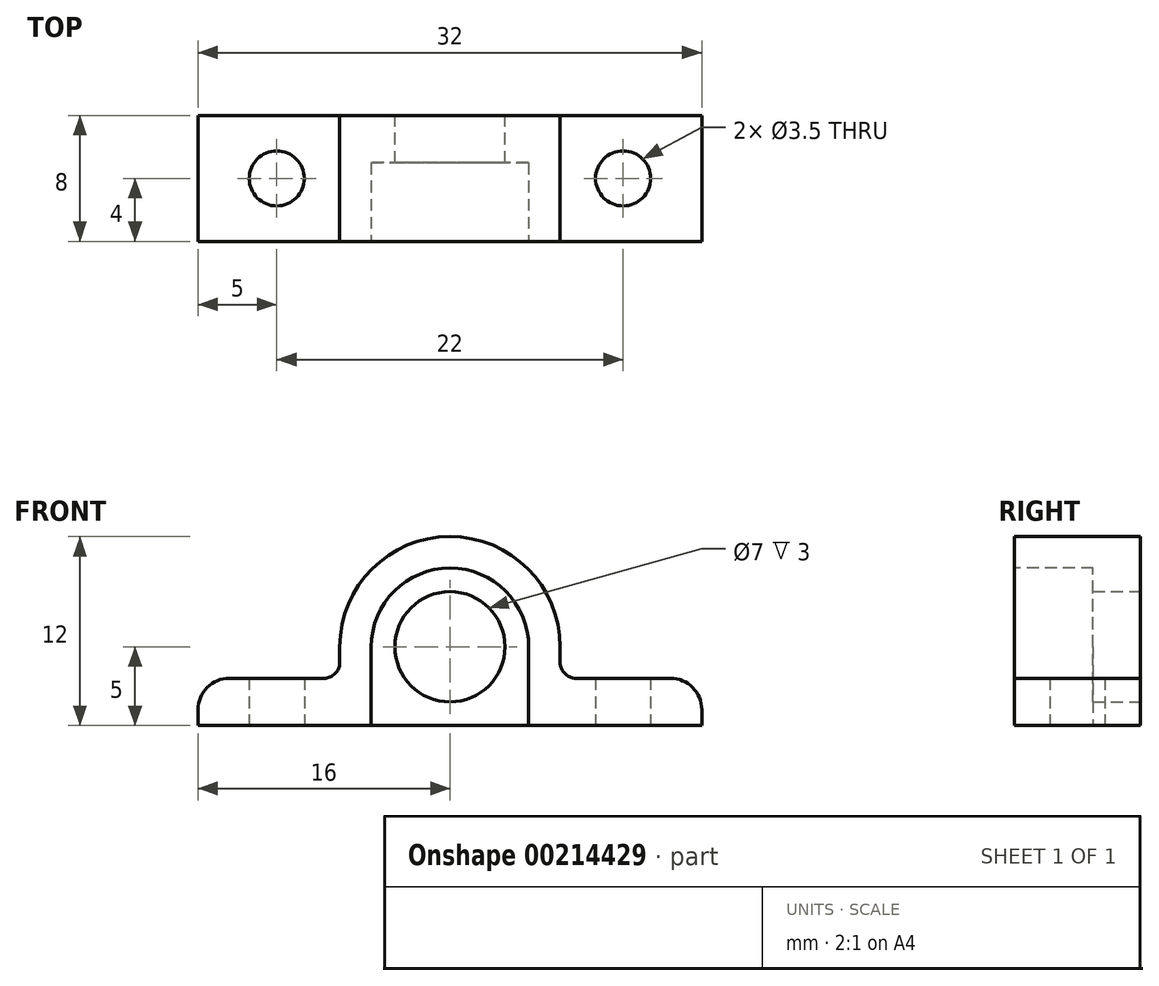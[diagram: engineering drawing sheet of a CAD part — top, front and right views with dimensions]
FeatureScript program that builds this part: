
annotation { "Feature Type Name" : "Feature", "Feature Type Description" : "" }
export const myFeature = defineFeature(function(context is Context, id is Id, definition is map)
    precondition{}
    {
        {
            var Q0;
            Q0=qCreatedBy(makeId("Front.planeOp"),FACE);
            var sketch = newSketch(context, id + "F0", { "sketchPlane" : qUnion([Q0])});
            skLineSegment(sketch, "E0.bottom", {"start": v(-16, 0) * mm, "end": v(16, 0) * mm});
            skLineSegment(sketch, "E0.top", {"start": v(0, 12) * mm, "end": v(0, 12) * mm});
            skLineSegment(sketch, "E0.left", {"start": v(-16, 0) * mm, "end": v(-16, 1) * mm});
            skLineSegment(sketch, "E0.right", {"start": v(16, 0) * mm, "end": v(16, 1) * mm});
            skCircle(sketch, "E1", {"center": v(0, 5) * mm, "radius": 3.5 * mm});
            skLineSegment(sketch, "E2.top", {"start": v(-14, 3) * mm, "end": v(-8, 3) * mm});
            skLineSegment(sketch, "E2.right", {"start": v(-7, 5) * mm, "end": v(-7, 4) * mm});
            skLineSegment(sketch, "E3.top", {"start": v(14, 3) * mm, "end": v(8, 3) * mm});
            skLineSegment(sketch, "E3.right", {"start": v(7, 5) * mm, "end": v(7, 4) * mm});
            skPoint(sketch, "E4.visualSharp", {"position": v(-7, 12) * mm});
            skArc(sketch, "E4.filletArc", {"start": v(0, 12) * mm, "mid": v(-4.95, 9.95) * mm, "end": v(-7, 5) * mm});
            skPoint(sketch, "E5.visualSharp", {"position": v(7, 12) * mm});
            skArc(sketch, "E5.filletArc", {"start": v(7, 5) * mm, "mid": v(4.95, 9.95) * mm, "end": v(0, 12) * mm});
            skPoint(sketch, "E6.visualSharp", {"position": v(-7, 3) * mm});
            skArc(sketch, "E6.filletArc", {"start": v(-8, 3) * mm, "mid": v(-7.3, 3.3) * mm, "end": v(-7, 4) * mm});
            skPoint(sketch, "E7.visualSharp", {"position": v(7, 3) * mm});
            skArc(sketch, "E7.filletArc", {"start": v(7, 4) * mm, "mid": v(7.3, 3.3) * mm, "end": v(8, 3) * mm});
            skPoint(sketch, "E8.visualSharp", {"position": v(-16, 3) * mm});
            skArc(sketch, "E8.filletArc", {"start": v(-14, 3) * mm, "mid": v(-15.41, 2.41) * mm, "end": v(-16, 1) * mm});
            skPoint(sketch, "E9.visualSharp", {"position": v(16, 3) * mm});
            skArc(sketch, "E9.filletArc", {"start": v(16, 1) * mm, "mid": v(15.41, 2.41) * mm, "end": v(14, 3) * mm});
            skSolve(sketch);
        }
        {
            var Q0;
            Q0=makeQuery(id+"F0.imprint","IMPRINT",FACE,{"disambiguationData":[TD([[makeQuery(id+"F0.imprint","IMPRINT",EDGE,{"derivedFrom":sQuery(id+"F0.wireOp",EDGE,"E0.bottom")}),1.0]])]});
            extrude(context, id + "F1", {"entities" : qUnion([Q0]), "depth" : 8 * mm});
        }
        {
            var Q0;
            Q0=makeQuery(id+"F1.opExtrude","SWEPT_FACE",FACE,{"disambiguationData":[OSD([sQuery(id+"F0.wireOp",EDGE,"E0.bottom")])]});
            var sketch = newSketch(context, id + "F2", { "sketchPlane" : qUnion([Q0])});
            skCircle(sketch, "E10", {"center": v(-11, 4) * mm, "radius": 1.75 * mm});
            skCircle(sketch, "E11", {"center": v(11, 4) * mm, "radius": 1.75 * mm});
            skSolve(sketch);
        }
        {
            var Q0;
            Q0 = qSketchRegion(id + "F2", true);
            extrude(context, id + "F3", {"entities" : qUnion([Q0]), "operationType" : NewBodyOperationType.REMOVE, "endBound" : BoundingType.THROUGH_ALL, "oppositeDirection" : true, "depth" : 25 * mm});
        }
        {
            var Q0;
            Q0=makeQuery(id+"F1.opExtrude","CAP_FACE",FACE,{"disambiguationData":[OSD([sQuery(id+"F0.wireOp",EDGE,"E0.bottom"),sQuery(id+"F0.wireOp",EDGE,"E0.left"),sQuery(id+"F0.wireOp",EDGE,"E0.right"),sQuery(id+"F0.wireOp",EDGE,"E1"),sQuery(id+"F0.wireOp",EDGE,"E2.top"),sQuery(id+"F0.wireOp",EDGE,"E2.right"),sQuery(id+"F0.wireOp",EDGE,"E3.top"),sQuery(id+"F0.wireOp",EDGE,"E3.right"),sQuery(id+"F0.wireOp",EDGE,"E4.filletArc"),sQuery(id+"F0.wireOp",EDGE,"E5.filletArc"),sQuery(id+"F0.wireOp",EDGE,"E6.filletArc"),sQuery(id+"F0.wireOp",EDGE,"E7.filletArc"),sQuery(id+"F0.wireOp",EDGE,"E8.filletArc"),sQuery(id+"F0.wireOp",EDGE,"E9.filletArc")])],"isStart":false});
            var sketch = newSketch(context, id + "F4", { "sketchPlane" : qUnion([Q0])});
            skArc(sketch, "E12", {"start": v(5, 5) * mm, "mid": v(0, 10) * mm, "end": v(-5, 5) * mm});
            skLineSegment(sketch, "E13", {"start": v(-5, 5) * mm, "end": v(-5, 0) * mm});
            skLineSegment(sketch, "E14", {"start": v(-5, 0) * mm, "end": v(5, 0) * mm});
            skLineSegment(sketch, "E15", {"start": v(5, 0) * mm, "end": v(5, 5) * mm});
            skSolve(sketch);
        }
        {
            var Q0;
            Q0 = qSketchRegion(id + "F4", true);
            extrude(context, id + "F5", {"entities" : qUnion([Q0]), "operationType" : NewBodyOperationType.REMOVE, "oppositeDirection" : true, "depth" : 5 * mm});
        }
    });
